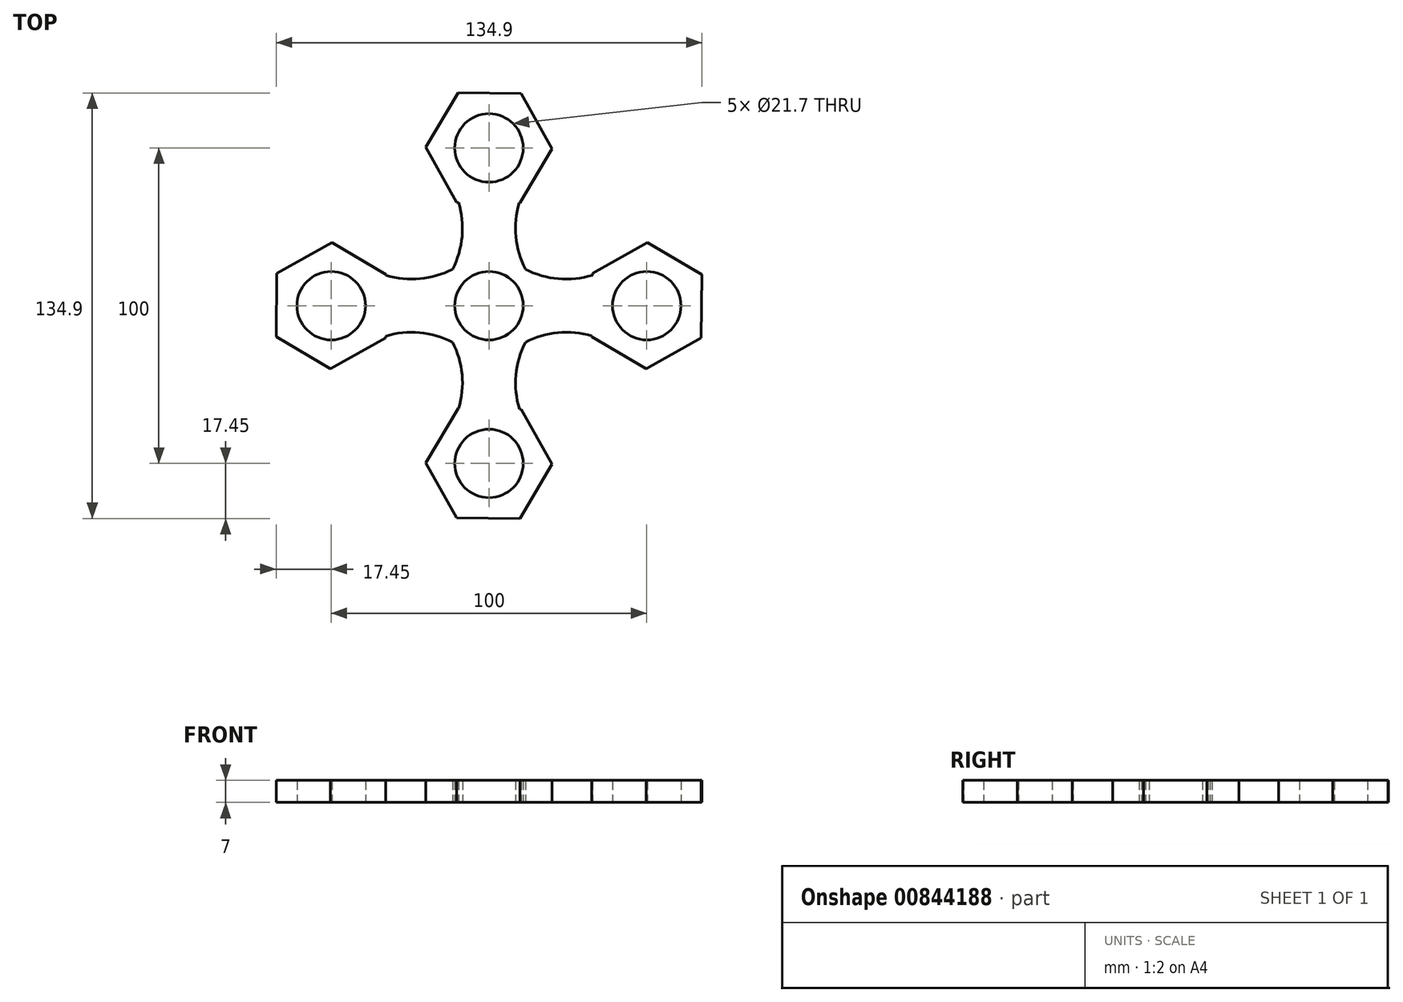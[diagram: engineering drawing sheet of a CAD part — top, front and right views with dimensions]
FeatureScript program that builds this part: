
annotation { "Feature Type Name" : "Feature", "Feature Type Description" : "" }
export const myFeature = defineFeature(function(context is Context, id is Id, definition is map)
    precondition{}
    {
        {
            var Q0;
            Q0=qCreatedBy(makeId("Top.planeOp"),FACE);
            var sketch = newSketch(context, id + "F0", { "sketchPlane" : qUnion([Q0])});
            skCircle(sketch, "E0", {"center": v(0, 0) * mm, "radius": 10.85 * mm});
            skCircle(sketch, "E1", {"center": v(-50, 0) * mm, "radius": 10.85 * mm});
            skPoint(sketch, "E2.0.midPoint", {"position": v(-63.62, 7.4) * mm});
            skLineSegment(sketch, "E3.trimOffspring", {"start": v(0, 0) * mm, "end": v(1.66, 0) * mm});
            skPoint(sketch, "E4.orphan", {"position": v(-66.02, 2.98) * mm});
            skPoint(sketch, "E2.1.start.orphan", {"position": v(-61.21, 11.83) * mm});
            skLineSegment(sketch, "E5.0", {"start": v(-67.23, 10.2) * mm, "end": v(-49.77, 20.02) * mm});
            skLineSegment(sketch, "E5.1", {"start": v(-49.77, 20.02) * mm, "end": v(-32.55, 9.81) * mm});
            skLineSegment(sketch, "E5.2", {"start": v(-32.55, 9.81) * mm, "end": v(-32.55, 9.59) * mm});
            skLineSegment(sketch, "E5.3", {"start": v(-32.77, -10.2) * mm, "end": v(-50.23, -20.02) * mm});
            skLineSegment(sketch, "E5.4", {"start": v(-50.23, -20.02) * mm, "end": v(-67.45, -9.81) * mm});
            skLineSegment(sketch, "E5.5", {"start": v(-67.45, -9.81) * mm, "end": v(-67.23, 10.2) * mm});
            skPoint(sketch, "E5.0.midPoint", {"position": v(-58.5, 15.11) * mm});
            skArc(sketch, "E6.trimOffspring", {"start": v(-32.77, -9.66) * mm, "mid": v(-21.98, -8.53) * mm, "end": v(-11.56, -11.56) * mm});
            skLineSegment(sketch, "E7.trimOffspring", {"start": v(-32.77, -9.66) * mm, "end": v(-32.77, -10.2) * mm});
            skArc(sketch, "E8.trimOffspring", {"start": v(-32.55, 9.59) * mm, "mid": v(-21.86, 8.54) * mm, "end": v(-11.56, 11.56) * mm});
            skLineSegment(sketch, "E9.1.0", {"start": v(-10.2, -67.23) * mm, "end": v(-20.02, -49.77) * mm});
            skPoint(sketch, "E9.1.1", {"position": v(-7.4, -63.62) * mm});
            skArc(sketch, "E9.1.2", {"start": v(-9.59, -32.55) * mm, "mid": v(-8.54, -21.86) * mm, "end": v(-11.56, -11.56) * mm});
            skPoint(sketch, "E9.1.3", {"position": v(-11.83, -61.21) * mm});
            skPoint(sketch, "E9.1.4", {"position": v(-15.11, -58.5) * mm});
            skPoint(sketch, "E9.1.5", {"position": v(-2.98, -66.02) * mm});
            skLineSegment(sketch, "E9.1.6", {"start": v(20.02, -50.23) * mm, "end": v(9.81, -67.45) * mm});
            skLineSegment(sketch, "E9.1.7", {"start": v(9.81, -67.45) * mm, "end": v(-10.2, -67.23) * mm});
            skLineSegment(sketch, "E9.1.8", {"start": v(-20.02, -49.77) * mm, "end": v(-9.81, -32.55) * mm});
            skCircle(sketch, "E9.1.9", {"center": v(0, -50) * mm, "radius": 10.85 * mm});
            skLineSegment(sketch, "E9.1.10", {"start": v(10.2, -32.77) * mm, "end": v(20.02, -50.23) * mm});
            skArc(sketch, "E9.1.11", {"start": v(9.66, -32.77) * mm, "mid": v(8.53, -21.98) * mm, "end": v(11.56, -11.56) * mm});
            skLineSegment(sketch, "E9.1.12", {"start": v(-9.81, -32.55) * mm, "end": v(-9.59, -32.55) * mm});
            skLineSegment(sketch, "E9.1.13", {"start": v(9.66, -32.77) * mm, "end": v(10.2, -32.77) * mm});
            skLineSegment(sketch, "E9.2.0", {"start": v(67.23, -10.2) * mm, "end": v(49.77, -20.02) * mm});
            skPoint(sketch, "E9.2.1", {"position": v(63.62, -7.4) * mm});
            skArc(sketch, "E9.2.2", {"start": v(32.55, -9.59) * mm, "mid": v(21.86, -8.54) * mm, "end": v(11.56, -11.56) * mm});
            skPoint(sketch, "E9.2.3", {"position": v(61.21, -11.83) * mm});
            skPoint(sketch, "E9.2.4", {"position": v(58.5, -15.11) * mm});
            skPoint(sketch, "E9.2.5", {"position": v(66.02, -2.98) * mm});
            skLineSegment(sketch, "E9.2.6", {"start": v(50.23, 20.02) * mm, "end": v(67.45, 9.81) * mm});
            skLineSegment(sketch, "E9.2.7", {"start": v(67.45, 9.81) * mm, "end": v(67.23, -10.2) * mm});
            skLineSegment(sketch, "E9.2.8", {"start": v(49.77, -20.02) * mm, "end": v(32.55, -9.81) * mm});
            skCircle(sketch, "E9.2.9", {"center": v(50, 0) * mm, "radius": 10.85 * mm});
            skLineSegment(sketch, "E9.2.10", {"start": v(32.77, 10.2) * mm, "end": v(50.23, 20.02) * mm});
            skArc(sketch, "E9.2.11", {"start": v(32.77, 9.66) * mm, "mid": v(21.98, 8.53) * mm, "end": v(11.56, 11.56) * mm});
            skLineSegment(sketch, "E9.2.12", {"start": v(32.55, -9.81) * mm, "end": v(32.55, -9.59) * mm});
            skLineSegment(sketch, "E9.2.13", {"start": v(32.77, 9.66) * mm, "end": v(32.77, 10.2) * mm});
            skLineSegment(sketch, "E9.3.0", {"start": v(10.2, 67.23) * mm, "end": v(20.02, 49.77) * mm});
            skPoint(sketch, "E9.3.1", {"position": v(7.4, 63.62) * mm});
            skArc(sketch, "E9.3.2", {"start": v(9.59, 32.55) * mm, "mid": v(8.54, 21.86) * mm, "end": v(11.56, 11.56) * mm});
            skPoint(sketch, "E9.3.3", {"position": v(11.83, 61.21) * mm});
            skPoint(sketch, "E9.3.4", {"position": v(15.11, 58.5) * mm});
            skPoint(sketch, "E9.3.5", {"position": v(2.98, 66.02) * mm});
            skLineSegment(sketch, "E9.3.6", {"start": v(-20.02, 50.23) * mm, "end": v(-9.81, 67.45) * mm});
            skLineSegment(sketch, "E9.3.7", {"start": v(-9.81, 67.45) * mm, "end": v(10.2, 67.23) * mm});
            skLineSegment(sketch, "E9.3.8", {"start": v(20.02, 49.77) * mm, "end": v(9.81, 32.55) * mm});
            skCircle(sketch, "E9.3.9", {"center": v(0, 50) * mm, "radius": 10.85 * mm});
            skLineSegment(sketch, "E9.3.10", {"start": v(-10.2, 32.77) * mm, "end": v(-20.02, 50.23) * mm});
            skArc(sketch, "E9.3.11", {"start": v(-9.66, 32.77) * mm, "mid": v(-8.53, 21.98) * mm, "end": v(-11.56, 11.56) * mm});
            skLineSegment(sketch, "E9.3.12", {"start": v(9.81, 32.55) * mm, "end": v(9.59, 32.55) * mm});
            skLineSegment(sketch, "E9.3.13", {"start": v(-9.66, 32.77) * mm, "end": v(-10.2, 32.77) * mm});
            skPoint(sketch, "E10.orphan", {"position": v(8.81, 13.18) * mm});
            skPoint(sketch, "E11.orphan", {"position": v(13.18, 8.81) * mm});
            skPoint(sketch, "E12.orphan", {"position": v(13.18, -8.81) * mm});
            skPoint(sketch, "E13.orphan", {"position": v(8.81, -13.18) * mm});
            skPoint(sketch, "E14.orphan", {"position": v(-8.81, -13.18) * mm});
            skPoint(sketch, "E15.orphan", {"position": v(-13.18, -8.81) * mm});
            skPoint(sketch, "E16.orphan", {"position": v(-13.18, 8.81) * mm});
            skPoint(sketch, "E17.orphan", {"position": v(-8.81, 13.18) * mm});
            skSolve(sketch);
        }
        {
            var Q0;
            Q0=makeQuery(id+"F0.imprint","IMPRINT",FACE,{"disambiguationData":[TD([[makeQuery(id+"F0.imprint","IMPRINT",EDGE,{"derivedFrom":sQuery(id+"F0.wireOp",EDGE,"E0")}),-1.0]])]});
            extrude(context, id + "F1", {"entities" : qUnion([Q0]), "depth" : 7 * mm, "offsetDistance" : 25 * mm});
        }
    });
